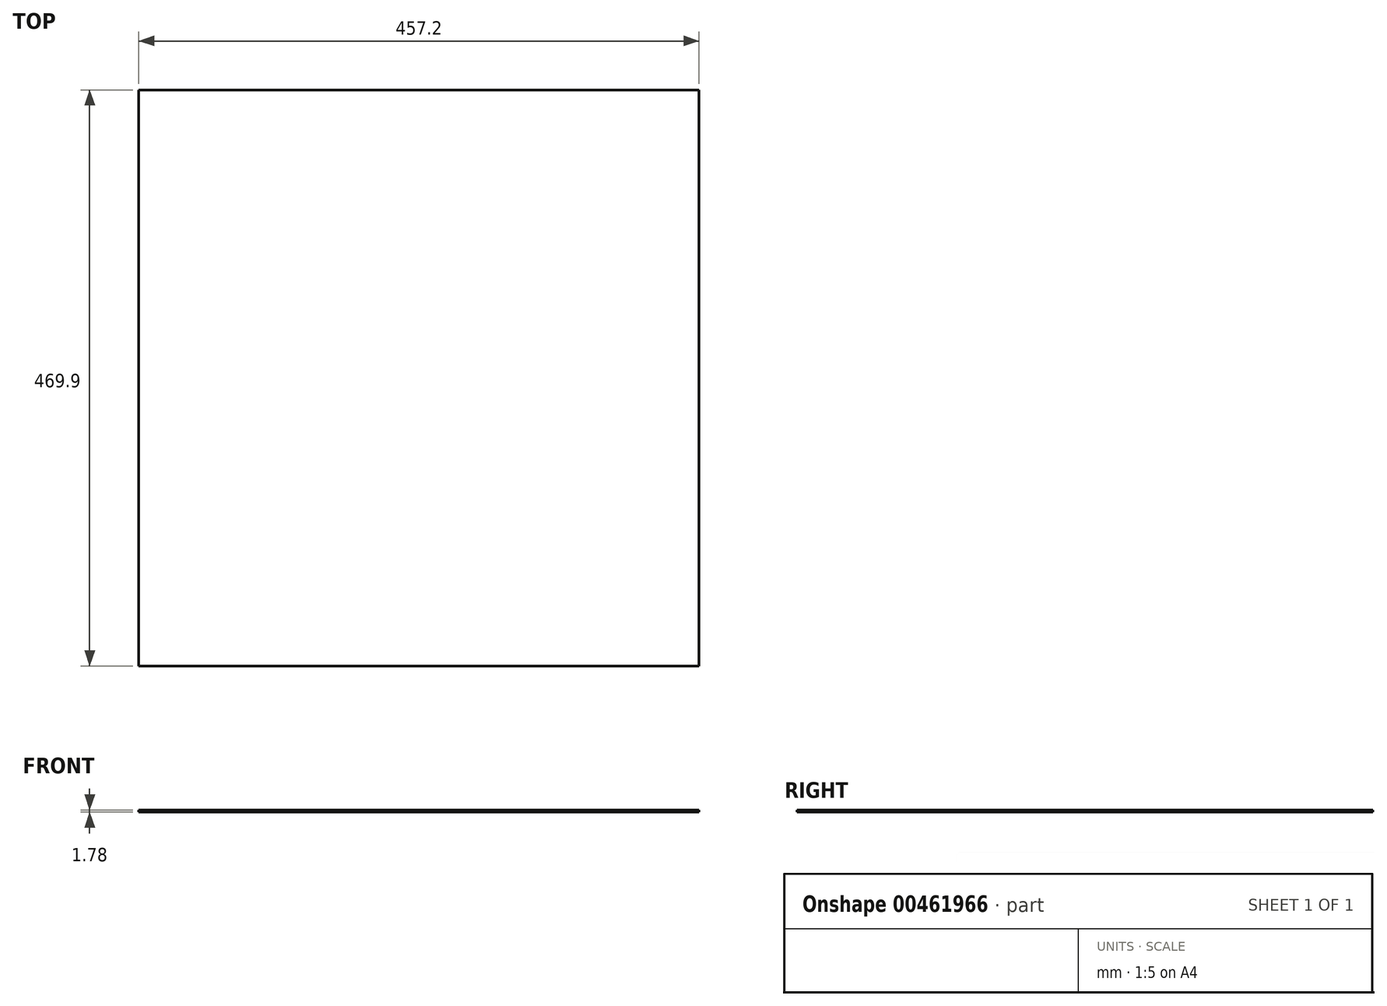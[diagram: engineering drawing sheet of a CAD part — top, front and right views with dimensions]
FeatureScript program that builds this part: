
annotation { "Feature Type Name" : "Feature", "Feature Type Description" : "" }
export const myFeature = defineFeature(function(context is Context, id is Id, definition is map)
    precondition{}
    {
        {
            var Q0;
            Q0=qCreatedBy(makeId("Top.planeOp"),FACE);
            var sketch = newSketch(context, id + "F0", { "sketchPlane" : qUnion([Q0])});
            skLineSegment(sketch, "E0.bottom", {"start": v(-228.6, 234.95) * mm, "end": v(228.6, 234.95) * mm});
            skLineSegment(sketch, "E0.top", {"start": v(-228.6, -234.95) * mm, "end": v(228.6, -234.95) * mm});
            skLineSegment(sketch, "E0.left", {"start": v(-228.6, 234.95) * mm, "end": v(-228.6, -234.95) * mm});
            skLineSegment(sketch, "E0.right", {"start": v(228.6, 234.95) * mm, "end": v(228.6, -234.95) * mm});
            skPoint(sketch, "E0.middle", {"position": v(0, 0) * mm});
            skSolve(sketch);
        }
        {
            var Q0;
            Q0=makeQuery(id+"F0.imprint","IMPRINT",FACE,{"disambiguationData":[TD([[makeQuery(id+"F0.imprint","IMPRINT",EDGE,{"derivedFrom":sQuery(id+"F0.wireOp",EDGE,"E0.bottom")}),-1.0]])]});
            extrude(context, id + "F1", {"entities" : qUnion([Q0]), "depth" : 1.78 * mm});
        }
    });
